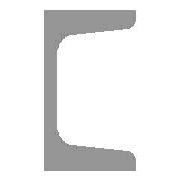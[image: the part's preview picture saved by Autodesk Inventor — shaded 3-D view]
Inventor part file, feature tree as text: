
AUTODESK INVENTOR PART (.ipt)
format: ipt  version: 2019 (Build 230136000, 136)  size: 156,672 bytes
history: native  units: mm (DEFAULTED — no unit token found)
features: other x4, sketch x3, plane x1
ambient origin geometry x8: Origin, YZ Plane, XZ Plane, XY Plane, X Axis, Y Axis, Z Axis, Center Point
bodies: Solid1 (feature_tree), Body (feature_tree)
feature tree (8):
  parser-record x1  (decoder bookkeeping rows leaked as tree rows — omitted from the tree; the rows remain in map.json)
  other  "Driven Length"
  other  "Start plane"
  other  "End plane"
  sketch  "Sketch5"  dims[d2=30.0mm d3=6.0mm d4=15.0mm d5=1.2mm d6=107.907368mm d7=0.0mm d23=6.0mm d24=3.0mm d25=0.0mm d26=-0.0mm d27=107.907368mm d28=90.0deg d29=107.907368mm d30=50.0mm d32=6.0mm d33=27.969585mm d34=3.0mm d35=1.469585mm d36=3.760764mm d37=1.089203mm d38=30.0mm d39=31.0mm d41=5.020861mm]
  sketch  "Sketch3"  dims[d0=6.0mm]
  plane  "Work Plane3"
  sketch  "Sketch4"  dims[d1=30.0mm]
